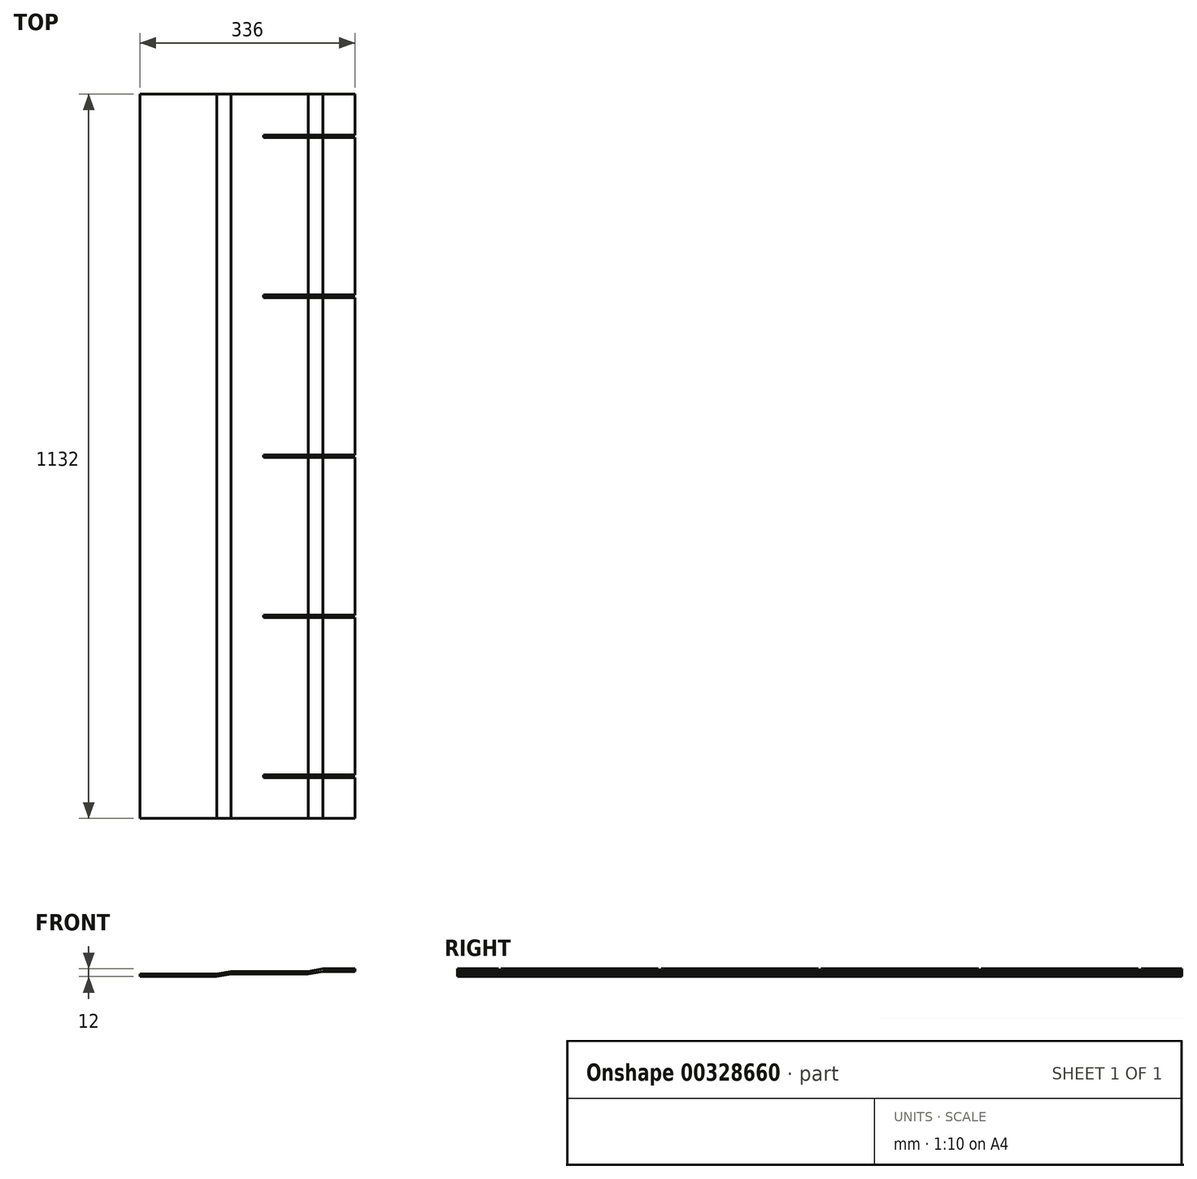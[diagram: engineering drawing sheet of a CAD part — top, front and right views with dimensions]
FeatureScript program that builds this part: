
annotation { "Feature Type Name" : "Feature", "Feature Type Description" : "" }
export const myFeature = defineFeature(function(context is Context, id is Id, definition is map)
    precondition{}
    {
        {
            var Q0;
            Q0=qCreatedBy(makeId("Front.planeOp"),FACE);
            var sketch = newSketch(context, id + "F0", { "sketchPlane" : qUnion([Q0])});
            skLineSegment(sketch, "E0.bottom", {"start": v(0, 0) * mm, "end": v(119.96, 0) * mm});
            skLineSegment(sketch, "E0.top", {"start": v(0, -4) * mm, "end": v(120.31, -4) * mm});
            skLineSegment(sketch, "E0.left", {"start": v(0, 0) * mm, "end": v(0, -4) * mm});
            skLineSegment(sketch, "E1", {"start": v(336, 4) * mm, "end": v(286, 4) * mm});
            skLineSegment(sketch, "E2", {"start": v(142.65, 4) * mm, "end": v(119.96, 0) * mm});
            skLineSegment(sketch, "E3", {"start": v(143, 0) * mm, "end": v(120.31, -4) * mm});
            skLineSegment(sketch, "E4.trimOffspring", {"start": v(143, 0) * mm, "end": v(263.31, 0) * mm});
            skLineSegment(sketch, "E5", {"start": v(336, 4) * mm, "end": v(336, 8) * mm});
            skLineSegment(sketch, "E6", {"start": v(336, 8) * mm, "end": v(285.65, 8) * mm});
            skLineSegment(sketch, "E7", {"start": v(285.65, 8) * mm, "end": v(262.96, 4) * mm});
            skLineSegment(sketch, "E8", {"start": v(263.31, 0) * mm, "end": v(286, 4) * mm});
            skLineSegment(sketch, "E9.trimOffspring", {"start": v(262.96, 4) * mm, "end": v(142.65, 4) * mm});
            skSolve(sketch);
        }
        {
            var Q0;
            Q0=qSketchRegion(id+"F0",true);
            extrude(context, id + "F1", {"entities" : qUnion([Q0]), "oppositeDirection" : true, "depth" : 1132 * mm});
        }
        {
            var Q0;
            Q0=makeQuery(id+"F1.opExtrude","SWEPT_FACE",FACE,{"disambiguationData":[OSD([sQuery(id+"F0.wireOp",EDGE,"E9.trimOffspring")])]});
            var sketch = newSketch(context, id + "F2", { "sketchPlane" : qUnion([Q0])});
            skLineSegment(sketch, "E10", {"start": v(193, 64) * mm, "end": v(193, 68) * mm});
            skLineSegment(sketch, "E11", {"start": v(193, 68) * mm, "end": v(336, 68) * mm});
            skLineSegment(sketch, "E12", {"start": v(336, 68) * mm, "end": v(336, 64) * mm});
            skLineSegment(sketch, "E13", {"start": v(336, 64) * mm, "end": v(193, 64) * mm});
            skPoint(sketch, "E14.endSnap0", {"position": v(202.8, 0) * mm});
            skLineSegment(sketch, "E15.0.1.0", {"start": v(336, 318) * mm, "end": v(336, 314) * mm});
            skLineSegment(sketch, "E15.0.1.1", {"start": v(193, 314) * mm, "end": v(193, 318) * mm});
            skLineSegment(sketch, "E15.0.1.2", {"start": v(193, 318) * mm, "end": v(336, 318) * mm});
            skLineSegment(sketch, "E15.0.1.3", {"start": v(336, 314) * mm, "end": v(193, 314) * mm});
            skLineSegment(sketch, "E15.0.2.0", {"start": v(336, 568) * mm, "end": v(336, 564) * mm});
            skLineSegment(sketch, "E15.0.2.1", {"start": v(193, 564) * mm, "end": v(193, 568) * mm});
            skLineSegment(sketch, "E15.0.2.2", {"start": v(193, 568) * mm, "end": v(336, 568) * mm});
            skLineSegment(sketch, "E15.0.2.3", {"start": v(336, 564) * mm, "end": v(193, 564) * mm});
            skLineSegment(sketch, "E15.direction1", {"start": v(193, 64) * mm, "end": v(193, 64) * mm});
            skLineSegment(sketch, "E15.direction2", {"start": v(193, 64) * mm, "end": v(193, 314) * mm, "construction": true});
            skLineSegment(sketch, "E16.0.0.3", {"start": v(336, 818) * mm, "end": v(336, 814) * mm});
            skLineSegment(sketch, "E16.3.0.3", {"start": v(193, 814) * mm, "end": v(193, 818) * mm});
            skLineSegment(sketch, "E16.6.0.3", {"start": v(193, 818) * mm, "end": v(336, 818) * mm});
            skLineSegment(sketch, "E16.9.0.3", {"start": v(336, 814) * mm, "end": v(193, 814) * mm});
            skLineSegment(sketch, "E17.0.0.4", {"start": v(336, 1068) * mm, "end": v(336, 1064) * mm});
            skLineSegment(sketch, "E17.3.0.4", {"start": v(193, 1064) * mm, "end": v(193, 1068) * mm});
            skLineSegment(sketch, "E17.6.0.4", {"start": v(193, 1068) * mm, "end": v(336, 1068) * mm});
            skLineSegment(sketch, "E17.9.0.4", {"start": v(336, 1064) * mm, "end": v(193, 1064) * mm});
            skSolve(sketch);
        }
        {
            var Q0;
            Q0=qSketchRegion(id+"F2",true);
            extrude(context, id + "F3", {"entities" : qUnion([Q0]), "operationType" : NewBodyOperationType.REMOVE, "endBound" : BoundingType.THROUGH_ALL, "oppositeDirection" : true, "depth" : 25 * mm, "hasSecondDirection" : true, "secondDirectionBound" : SecondDirectionBoundingType.THROUGH_ALL, "secondDirectionOppositeDirection" : false, "secondDirectionDepth" : 25 * mm});
        }
    });
